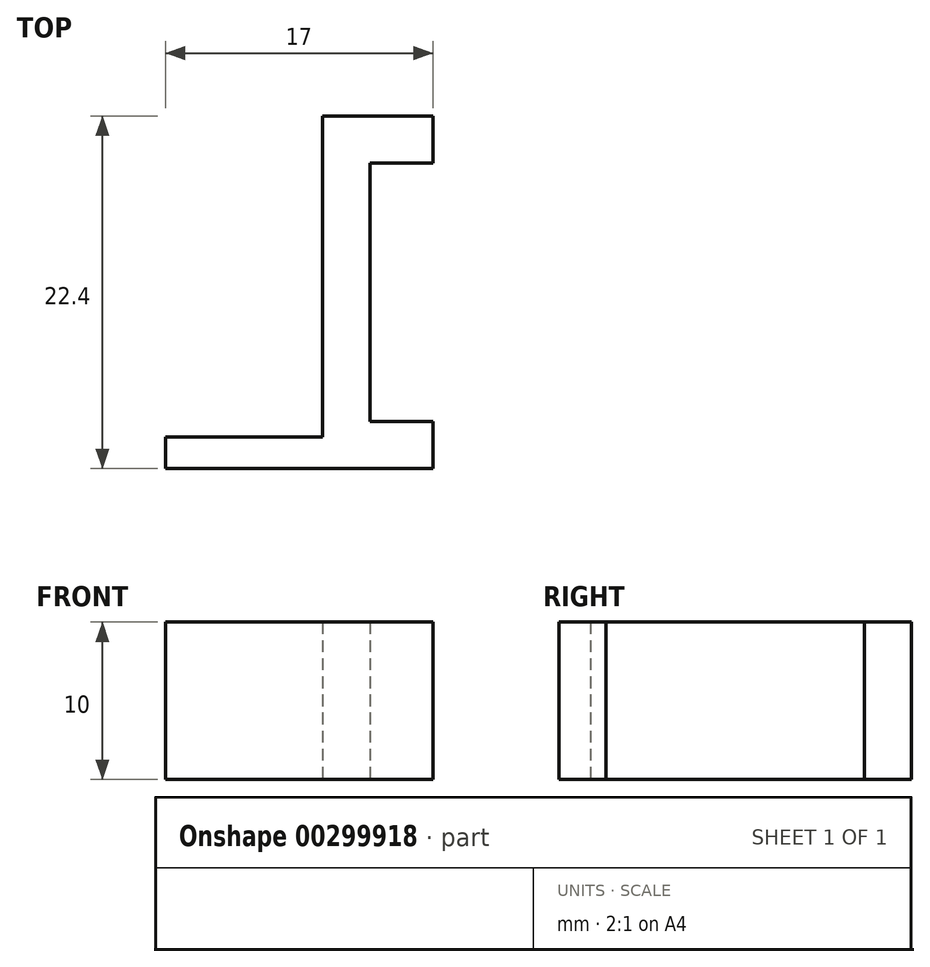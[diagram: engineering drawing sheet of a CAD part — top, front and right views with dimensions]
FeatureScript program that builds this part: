
annotation { "Feature Type Name" : "Feature", "Feature Type Description" : "" }
export const myFeature = defineFeature(function(context is Context, id is Id, definition is map)
    precondition{}
    {
        {
            var Q0;
            Q0=qCreatedBy(makeId("Top.planeOp"),FACE);
            var sketch = newSketch(context, id + "F0", { "sketchPlane" : qUnion([Q0])});
            skLineSegment(sketch, "E0", {"start": v(0, 0) * mm, "end": v(0, 2) * mm});
            skLineSegment(sketch, "E1", {"start": v(0, 2) * mm, "end": v(10, 2) * mm});
            skLineSegment(sketch, "E2", {"start": v(10, 2) * mm, "end": v(10, 22.4) * mm});
            skLineSegment(sketch, "E3", {"start": v(10, 22.4) * mm, "end": v(17, 22.4) * mm});
            skLineSegment(sketch, "E4", {"start": v(17, 22.4) * mm, "end": v(17, 19.4) * mm});
            skLineSegment(sketch, "E5", {"start": v(17, 19.4) * mm, "end": v(13, 19.4) * mm});
            skLineSegment(sketch, "E6", {"start": v(13, 19.4) * mm, "end": v(13, 3) * mm});
            skLineSegment(sketch, "E7", {"start": v(13, 3) * mm, "end": v(17, 3) * mm});
            skLineSegment(sketch, "E8", {"start": v(17, 3) * mm, "end": v(17, 0) * mm});
            skLineSegment(sketch, "E9", {"start": v(17, 0) * mm, "end": v(0, 0) * mm});
            skLineSegment(sketch, "E10", {"start": v(17, 3) * mm, "end": v(17, 19.4) * mm, "construction": true});
            skSolve(sketch);
        }
        {
            var Q0;
            Q0=qSketchRegion(id+"F0",true);
            extrude(context, id + "F1", {"entities" : qUnion([Q0]), "depth" : 10 * mm});
        }
    });
